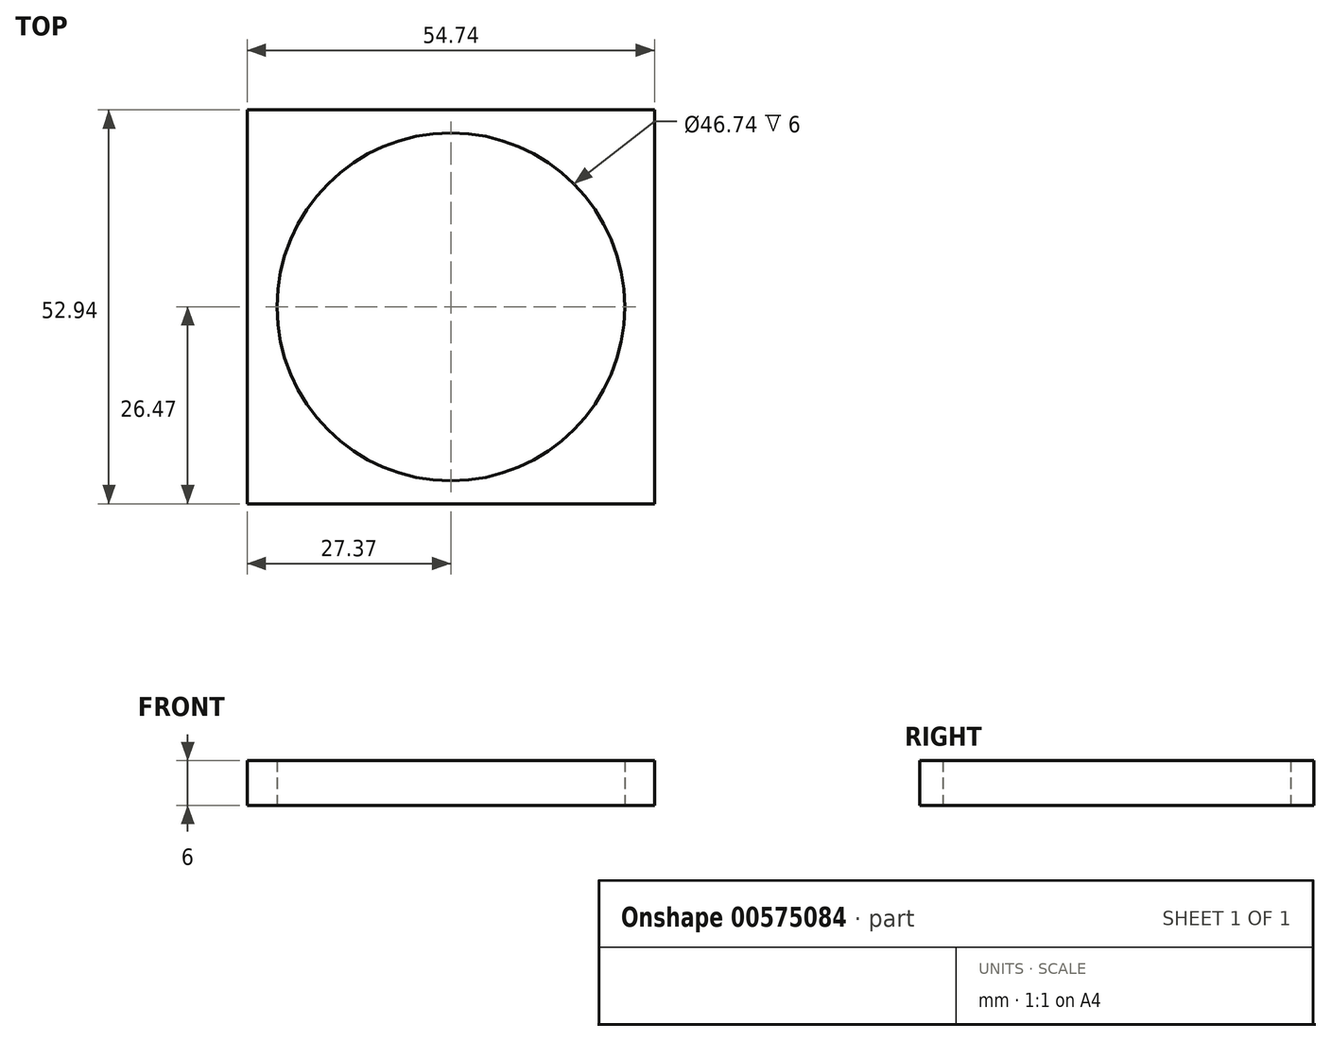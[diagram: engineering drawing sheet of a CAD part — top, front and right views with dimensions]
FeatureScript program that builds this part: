
annotation { "Feature Type Name" : "Feature", "Feature Type Description" : "" }
export const myFeature = defineFeature(function(context is Context, id is Id, definition is map)
    precondition{}
    {
        {
            var Q0;
            Q0=qCreatedBy(makeId("Top.planeOp"),FACE);
            var sketch = newSketch(context, id + "F0", { "sketchPlane" : qUnion([Q0])});
            skLineSegment(sketch, "E0.bottom", {"start": v(27.37, 26.47) * mm, "end": v(-27.37, 26.47) * mm});
            skLineSegment(sketch, "E0.top", {"start": v(27.37, -26.47) * mm, "end": v(-27.37, -26.47) * mm});
            skLineSegment(sketch, "E0.left", {"start": v(27.37, 26.47) * mm, "end": v(27.37, -26.47) * mm});
            skLineSegment(sketch, "E0.right", {"start": v(-27.37, 26.47) * mm, "end": v(-27.37, -26.47) * mm});
            skPoint(sketch, "E0.middle", {"position": v(0, 0) * mm});
            skCircle(sketch, "E1", {"center": v(0, 0) * mm, "radius": 23.37 * mm});
            skSolve(sketch);
        }
        {
            var Q0;
            Q0 = qSketchRegion(id + "F0", true);
            extrude(context, id + "F1", {"entities" : qUnion([Q0]), "depth" : 6 * mm, "offsetDistance" : 25.4 * mm});
        }
    });
